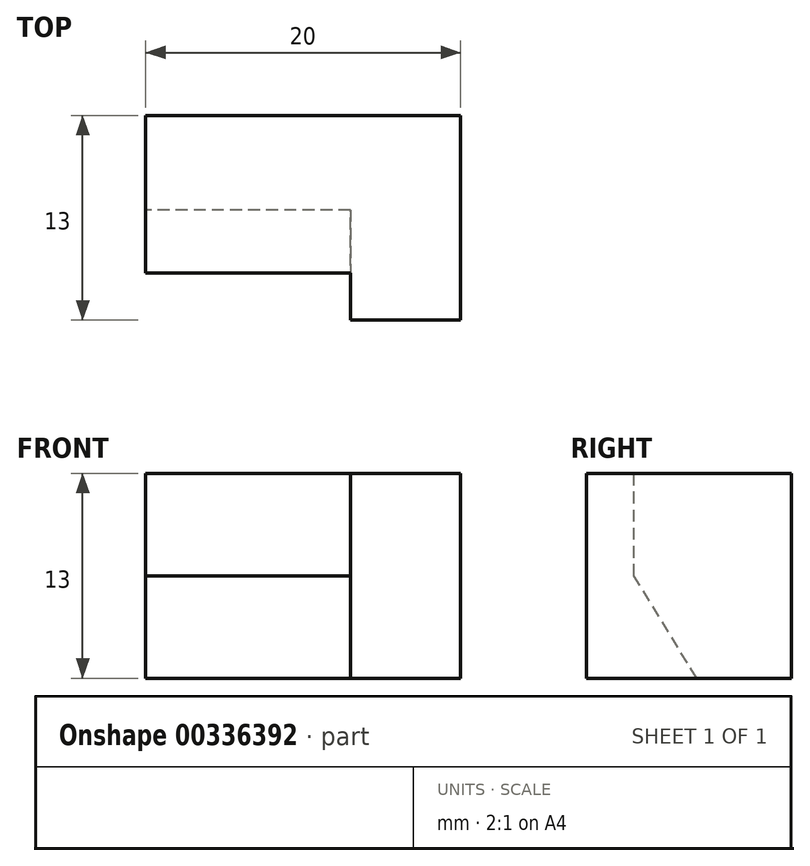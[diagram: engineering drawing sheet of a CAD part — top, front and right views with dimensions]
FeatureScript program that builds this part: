
annotation { "Feature Type Name" : "Feature", "Feature Type Description" : "" }
export const myFeature = defineFeature(function(context is Context, id is Id, definition is map)
    precondition{}
    {
        {
            var Q0;
            Q0=qCreatedBy(makeId("Top.planeOp"),FACE);
            var sketch = newSketch(context, id + "F0", { "sketchPlane" : qUnion([Q0])});
            skLineSegment(sketch, "E0.bottom", {"start": v(0, 0) * mm, "end": v(20, 0) * mm});
            skLineSegment(sketch, "E0.top", {"start": v(0, 13) * mm, "end": v(20, 13) * mm});
            skLineSegment(sketch, "E0.left", {"start": v(0, 0) * mm, "end": v(0, 13) * mm});
            skLineSegment(sketch, "E0.right", {"start": v(20, 0) * mm, "end": v(20, 13) * mm});
            skSolve(sketch);
        }
        {
            var Q0;
            Q0 = qSketchRegion(id + "F0", true);
            extrude(context, id + "F1", {"entities" : qUnion([Q0]), "depth" : 13 * mm});
        }
        {
            var Q0;
            Q0=makeQuery(id+"F1.opExtrude","SWEPT_FACE",FACE,{"disambiguationData":[OSD([sQuery(id+"F0.wireOp",EDGE,"E0.left")])]});
            var sketch = newSketch(context, id + "F2", { "sketchPlane" : qUnion([Q0])});
            skLineSegment(sketch, "E1", {"start": v(-3, 13) * mm, "end": v(0, 13) * mm});
            skLineSegment(sketch, "E2", {"start": v(0, 13) * mm, "end": v(0, 0) * mm});
            skLineSegment(sketch, "E3", {"start": v(0, 0) * mm, "end": v(-7, 0) * mm});
            skLineSegment(sketch, "E4", {"start": v(-7, 0) * mm, "end": v(-3, 6.5) * mm});
            skLineSegment(sketch, "E5", {"start": v(-3, 6.5) * mm, "end": v(-3, 13) * mm});
            skSolve(sketch);
        }
        {
            var Q0;
            Q0 = qSketchRegion(id + "F2", true);
            extrude(context, id + "F3", {"entities" : qUnion([Q0]), "operationType" : NewBodyOperationType.REMOVE, "oppositeDirection" : true, "depth" : 13 * mm});
        }
    });
